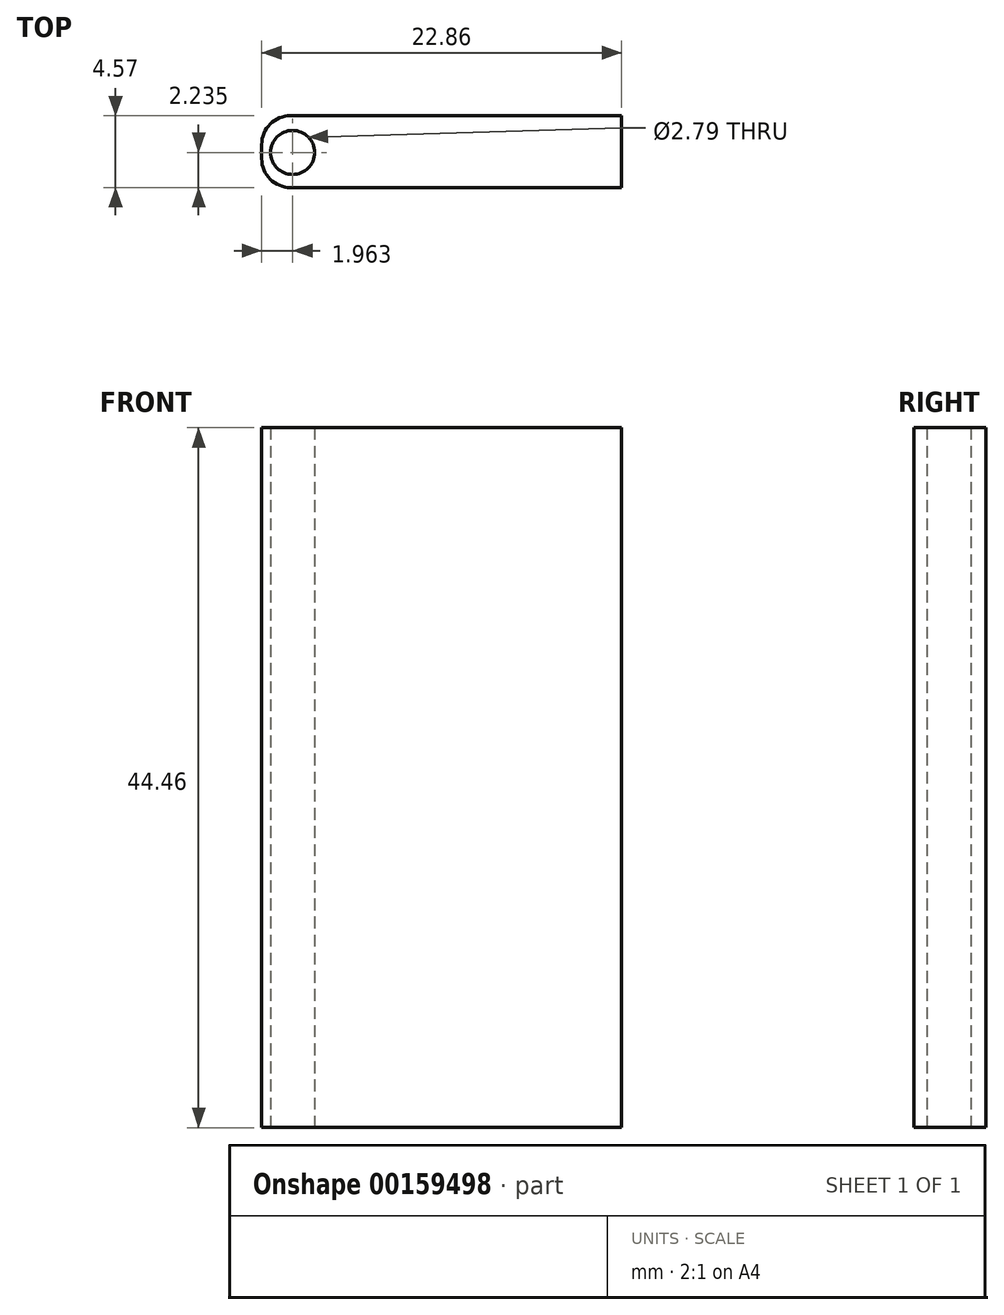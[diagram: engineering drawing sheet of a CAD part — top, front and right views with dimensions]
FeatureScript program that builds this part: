
annotation { "Feature Type Name" : "Feature", "Feature Type Description" : "" }
export const myFeature = defineFeature(function(context is Context, id is Id, definition is map)
    precondition{}
    {
        {
            var Q0;
            Q0=qCreatedBy(makeId("Front.planeOp"),FACE);
            var sketch = newSketch(context, id + "F0", { "sketchPlane" : qUnion([Q0])});
            skLineSegment(sketch, "E0.bottom", {"start": v(11.43, -22.23) * mm, "end": v(-11.43, -22.23) * mm});
            skLineSegment(sketch, "E0.top", {"start": v(11.43, 22.23) * mm, "end": v(-11.43, 22.23) * mm});
            skLineSegment(sketch, "E0.left", {"start": v(11.43, -22.23) * mm, "end": v(11.43, 22.23) * mm});
            skLineSegment(sketch, "E0.right", {"start": v(-11.43, -22.23) * mm, "end": v(-11.43, 22.23) * mm});
            skPoint(sketch, "E0.middle", {"position": v(0, 0) * mm});
            skSolve(sketch);
        }
        {
            var Q0;
            Q0 = qSketchRegion(id + "F0", true);
            extrude(context, id + "F1", {"entities" : qUnion([Q0]), "depth" : 5.08 * mm, "hasSecondDirection" : true, "secondDirectionOppositeDirection" : false, "secondDirectionDepth" : 0.5 * mm});
        }
        {
            var Q0;
            Q0=qCreatedBy(makeId("Top.planeOp"),FACE);
            var sketch = newSketch(context, id + "F2", { "sketchPlane" : qUnion([Q0])});
            skCircle(sketch, "E1", {"center": v(-9.47, -2.84) * mm, "radius": 1.4 * mm});
            skSolve(sketch);
        }
        {
            var Q0;
            Q0 = qSketchRegion(id + "F2", true);
            extrude(context, id + "F3", {"entities" : qUnion([Q0]), "operationType" : NewBodyOperationType.REMOVE, "depth" : 25.4 * mm, "hasSecondDirection" : true, "secondDirectionOppositeDirection" : true, "secondDirectionDepth" : 25.4 * mm});
        }
        {
            var Q0;
            Q0=makeQuery(id+"F1.opExtrude","CAP_EDGE",EDGE,{"disambiguationData":[OSD([sQuery(id+"F0.wireOp",EDGE,"E0.right")])],"isStart":true});
            fillet(context, id + "F4", {"entities" : qUnion([Q0]), "radius" : 1.84 * mm, "tangentPropagation" : true, "allowEdgeOverflow" : false});
        }
        {
            var Q0;
            Q0=makeQuery(id+"F1.opExtrude","CAP_EDGE",EDGE,{"disambiguationData":[OSD([sQuery(id+"F0.wireOp",EDGE,"E0.right")])],"isStart":false});
            fillet(context, id + "F5", {"entities" : qUnion([Q0]), "radius" : 1.84 * mm, "tangentPropagation" : true, "allowEdgeOverflow" : false});
        }
    });
